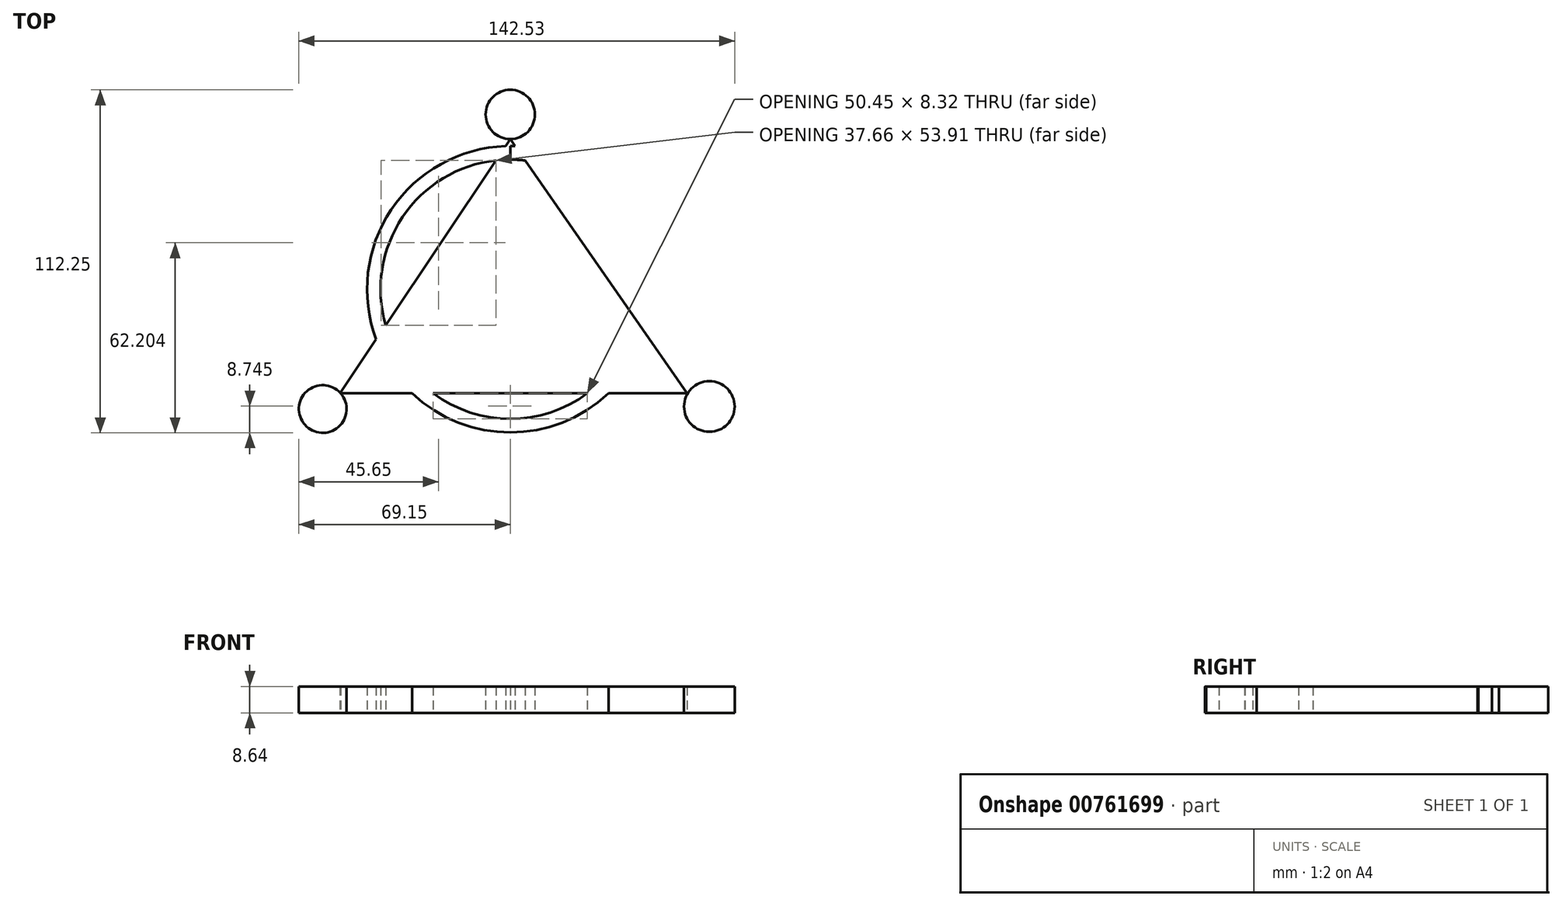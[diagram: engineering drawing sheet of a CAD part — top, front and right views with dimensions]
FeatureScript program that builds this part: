
annotation { "Feature Type Name" : "Feature", "Feature Type Description" : "" }
export const myFeature = defineFeature(function(context is Context, id is Id, definition is map)
    precondition{}
    {
        {
            var Q0;
            Q0=qCreatedBy(makeId("Top.planeOp"),FACE);
            var sketch = newSketch(context, id + "F0", { "sketchPlane" : qUnion([Q0])});
            skLineSegment(sketch, "E0", {"start": v(-55.71, -38.8) * mm, "end": v(46.31, -38.8) * mm});
            skLineSegment(sketch, "E1", {"start": v(-55.71, -38.8) * mm, "end": v(0, 44.44) * mm});
            skLineSegment(sketch, "E2", {"start": v(0, 44.44) * mm, "end": v(57.86, -38.8) * mm});
            skLineSegment(sketch, "E3", {"start": v(46.31, -38.8) * mm, "end": v(57.86, -38.8) * mm});
            skLineSegment(sketch, "E4", {"start": v(0, 44.44) * mm, "end": v(0, 52.49) * mm});
            skCircle(sketch, "E5", {"center": v(0, 52.49) * mm, "radius": 8.06 * mm});
            skLineSegment(sketch, "E6", {"start": v(57.86, -38.8) * mm, "end": v(65.1, -43.1) * mm});
            skCircle(sketch, "E7", {"center": v(65.1, -43.1) * mm, "radius": 8.27 * mm});
            skLineSegment(sketch, "E8", {"start": v(-55.71, -38.8) * mm, "end": v(-61.35, -43.9) * mm});
            skCircle(sketch, "E9", {"center": v(-61.35, -43.9) * mm, "radius": 7.8 * mm});
            skCircle(sketch, "E10", {"center": v(0, -4.7) * mm, "radius": 42.42 * mm});
            skCircle(sketch, "E11", {"center": v(0, -4.7) * mm, "radius": 46.84 * mm});
            skLineSegment(sketch, "E12", {"start": v(0, 44.44) * mm, "end": v(0, -38.8) * mm});
            skSolve(sketch);
        }
        {
            var Q0;
            {var subQ1=sQuery(id+"F0.wireOp",EDGE,"E0");var subQ6=sQuery(id+"F0.wireOp",EDGE,"E12");var subQ8=makeQuery(id+"F0.imprint","INTERSECT",VERTEX,{"derivedFrom":[subQ1,subQ6]});Q0=makeQuery(id+"F0.imprint","IMPRINT",FACE,{"disambiguationData":[TD([[makeQuery(id+"F0.imprint","IMPRINT",EDGE,{"disambiguationData":[TD([[subQ8,-1.0]])],"derivedFrom":subQ1}),1.0]])]});}
            var Q1;
            {var subQ1=sQuery(id+"F0.wireOp",EDGE,"E0");var subQ6=sQuery(id+"F0.wireOp",EDGE,"E12");var subQ8=makeQuery(id+"F0.imprint","INTERSECT",VERTEX,{"derivedFrom":[subQ1,subQ6]});Q1=makeQuery(id+"F0.imprint","IMPRINT",FACE,{"disambiguationData":[TD([[makeQuery(id+"F0.imprint","IMPRINT",EDGE,{"disambiguationData":[TD([[subQ8,1.0]])],"derivedFrom":subQ1}),1.0]])]});}
            var Q2;
            {var subQ0=sQuery(id+"F0.wireOp",EDGE,"E11");var subQ1=sQuery(id+"F0.wireOp",EDGE,"E1");var subQ2=makeQuery(id+"F0.imprint","INTERSECT",VERTEX,{"disambiguationData":[OD(1.0)],"derivedFrom":[subQ1,subQ0]});Q2=makeQuery(id+"F0.imprint","IMPRINT",FACE,{"disambiguationData":[TD([[makeQuery(id+"F0.imprint","IMPRINT",EDGE,{"disambiguationData":[TD([[subQ2,1.0]])],"derivedFrom":subQ1}),-1.0]])]});}
            var Q3;
            {var subQ0=sQuery(id+"F0.wireOp",EDGE,"E11");var subQ1=sQuery(id+"F0.wireOp",EDGE,"E2");var subQ2=makeQuery(id+"F0.imprint","INTERSECT",VERTEX,{"disambiguationData":[OD(0.0)],"derivedFrom":[subQ1,subQ0]});Q3=makeQuery(id+"F0.imprint","IMPRINT",FACE,{"disambiguationData":[TD([[makeQuery(id+"F0.imprint","IMPRINT",EDGE,{"disambiguationData":[TD([[subQ2,-1.0]])],"derivedFrom":subQ1}),-1.0]])]});}
            var Q4;
            {var subQ0=sQuery(id+"F0.wireOp",EDGE,"E11");var subQ1=sQuery(id+"F0.wireOp",EDGE,"E1");var subQ2=makeQuery(id+"F0.imprint","INTERSECT",VERTEX,{"disambiguationData":[OD(1.0)],"derivedFrom":[subQ1,subQ0]});Q4=makeQuery(id+"F0.imprint","IMPRINT",FACE,{"disambiguationData":[TD([[makeQuery(id+"F0.imprint","IMPRINT",EDGE,{"disambiguationData":[TD([[subQ2,-1.0]])],"derivedFrom":subQ1}),-1.0]])]});}
            var Q5;
            {var subQ0=sQuery(id+"F0.wireOp",EDGE,"E5");var subQ1=sQuery(id+"F0.wireOp",EDGE,"E2");var subQ2=makeQuery(id+"F0.imprint","INTERSECT",VERTEX,{"derivedFrom":[subQ1,subQ0]});Q5=makeQuery(id+"F0.imprint","IMPRINT",FACE,{"disambiguationData":[TD([[makeQuery(id+"F0.imprint","IMPRINT",EDGE,{"disambiguationData":[TD([[subQ2,-1.0]])],"derivedFrom":subQ1}),-1.0]])]});}
            var Q6;
            {var subQ1=sQuery(id+"F0.wireOp",EDGE,"E1");var subQ3=sQuery(id+"F0.wireOp",EDGE,"E5");var subQ4=makeQuery(id+"F0.imprint","INTERSECT",VERTEX,{"derivedFrom":[subQ1,subQ3]});Q6=makeQuery(id+"F0.imprint","IMPRINT",FACE,{"disambiguationData":[TD([[makeQuery(id+"F0.imprint","IMPRINT",EDGE,{"disambiguationData":[TD([[subQ4,1.0]])],"derivedFrom":subQ3}),1.0]])]});}
            var Q7;
            {var subQ0=sQuery(id+"F0.wireOp",EDGE,"E11");var subQ1=sQuery(id+"F0.wireOp",EDGE,"E2");var subQ2=makeQuery(id+"F0.imprint","INTERSECT",VERTEX,{"disambiguationData":[OD(0.0)],"derivedFrom":[subQ1,subQ0]});Q7=makeQuery(id+"F0.imprint","IMPRINT",FACE,{"disambiguationData":[TD([[makeQuery(id+"F0.imprint","IMPRINT",EDGE,{"disambiguationData":[TD([[subQ2,-1.0]])],"derivedFrom":subQ1}),1.0]])]});}
            var Q8;
            {var subQ0=sQuery(id+"F0.wireOp",EDGE,"E11");var subQ1=sQuery(id+"F0.wireOp",EDGE,"E0");var subQ2=makeQuery(id+"F0.imprint","INTERSECT",VERTEX,{"disambiguationData":[OD(1.0)],"derivedFrom":[subQ1,subQ0]});Q8=makeQuery(id+"F0.imprint","IMPRINT",FACE,{"disambiguationData":[TD([[makeQuery(id+"F0.imprint","IMPRINT",EDGE,{"disambiguationData":[TD([[subQ2,1.0]])],"derivedFrom":subQ1}),1.0]])]});}
            var Q9;
            {var subQ0=sQuery(id+"F0.wireOp",EDGE,"E3");Q9=makeQuery(id+"F0.imprint","IMPRINT",FACE,{"disambiguationData":[TD([[makeQuery(id+"F0.imprint","IMPRINT",EDGE,{"derivedFrom":subQ0}),1.0]])]});}
            var Q10;
            Q10=makeQuery(id+"F0.imprint","IMPRINT",FACE,{"disambiguationData":[TD([[makeQuery(id+"F0.imprint","IMPRINT",EDGE,{"derivedFrom":sQuery(id+"F0.wireOp",EDGE,"E7")}),1.0]])]});
            var Q11;
            {var subQ0=sQuery(id+"F0.wireOp",EDGE,"E11");var subQ1=sQuery(id+"F0.wireOp",EDGE,"E0");var subQ2=makeQuery(id+"F0.imprint","INTERSECT",VERTEX,{"disambiguationData":[OD(0.0)],"derivedFrom":[subQ1,subQ0]});Q11=makeQuery(id+"F0.imprint","IMPRINT",FACE,{"disambiguationData":[TD([[makeQuery(id+"F0.imprint","IMPRINT",EDGE,{"disambiguationData":[TD([[subQ2,-1.0]])],"derivedFrom":subQ1}),-1.0]])]});}
            var Q12;
            {var subQ0=sQuery(id+"F0.wireOp",EDGE,"E9");var subQ1=sQuery(id+"F0.wireOp",EDGE,"E0");var subQ2=makeQuery(id+"F0.imprint","INTERSECT",VERTEX,{"derivedFrom":[subQ1,subQ0]});Q12=makeQuery(id+"F0.imprint","IMPRINT",FACE,{"disambiguationData":[TD([[makeQuery(id+"F0.imprint","IMPRINT",EDGE,{"disambiguationData":[TD([[subQ2,-1.0]])],"derivedFrom":subQ1}),1.0]])]});}
            var Q13;
            {var subQ0=sQuery(id+"F0.wireOp",EDGE,"E11");var subQ1=sQuery(id+"F0.wireOp",EDGE,"E0");var subQ2=makeQuery(id+"F0.imprint","INTERSECT",VERTEX,{"disambiguationData":[OD(0.0)],"derivedFrom":[subQ1,subQ0]});Q13=makeQuery(id+"F0.imprint","IMPRINT",FACE,{"disambiguationData":[TD([[makeQuery(id+"F0.imprint","IMPRINT",EDGE,{"disambiguationData":[TD([[subQ2,-1.0]])],"derivedFrom":subQ1}),1.0]])]});}
            var Q14;
            {var subQ0=sQuery(id+"F0.wireOp",EDGE,"E1");var subQ1=sQuery(id+"F0.wireOp",EDGE,"E0");var subQ2=makeQuery(id+"F0.imprint","INTERSECT",VERTEX,{"derivedFrom":[subQ1,subQ0]});Q14=makeQuery(id+"F0.imprint","IMPRINT",FACE,{"disambiguationData":[TD([[makeQuery(id+"F0.imprint","IMPRINT",EDGE,{"disambiguationData":[TD([[subQ2,-1.0]])],"derivedFrom":subQ1}),-1.0]])]});}
            var Q15;
            {var subQ0=sQuery(id+"F0.wireOp",EDGE,"E11");var subQ1=sQuery(id+"F0.wireOp",EDGE,"E1");var subQ2=makeQuery(id+"F0.imprint","INTERSECT",VERTEX,{"disambiguationData":[OD(0.0)],"derivedFrom":[subQ1,subQ0]});Q15=makeQuery(id+"F0.imprint","IMPRINT",FACE,{"disambiguationData":[TD([[makeQuery(id+"F0.imprint","IMPRINT",EDGE,{"disambiguationData":[TD([[subQ2,-1.0]])],"derivedFrom":subQ1}),1.0]])]});}
            extrude(context, id + "F1", {"entities" : qUnion([Q0, Q1, Q2, Q3, Q4, Q5, Q6, Q7, Q8, Q9, Q10, Q11, Q12, Q13, Q14, Q15]), "depth" : 8.64 * mm, "offsetDistance" : 25.4 * mm});
        }
    });
